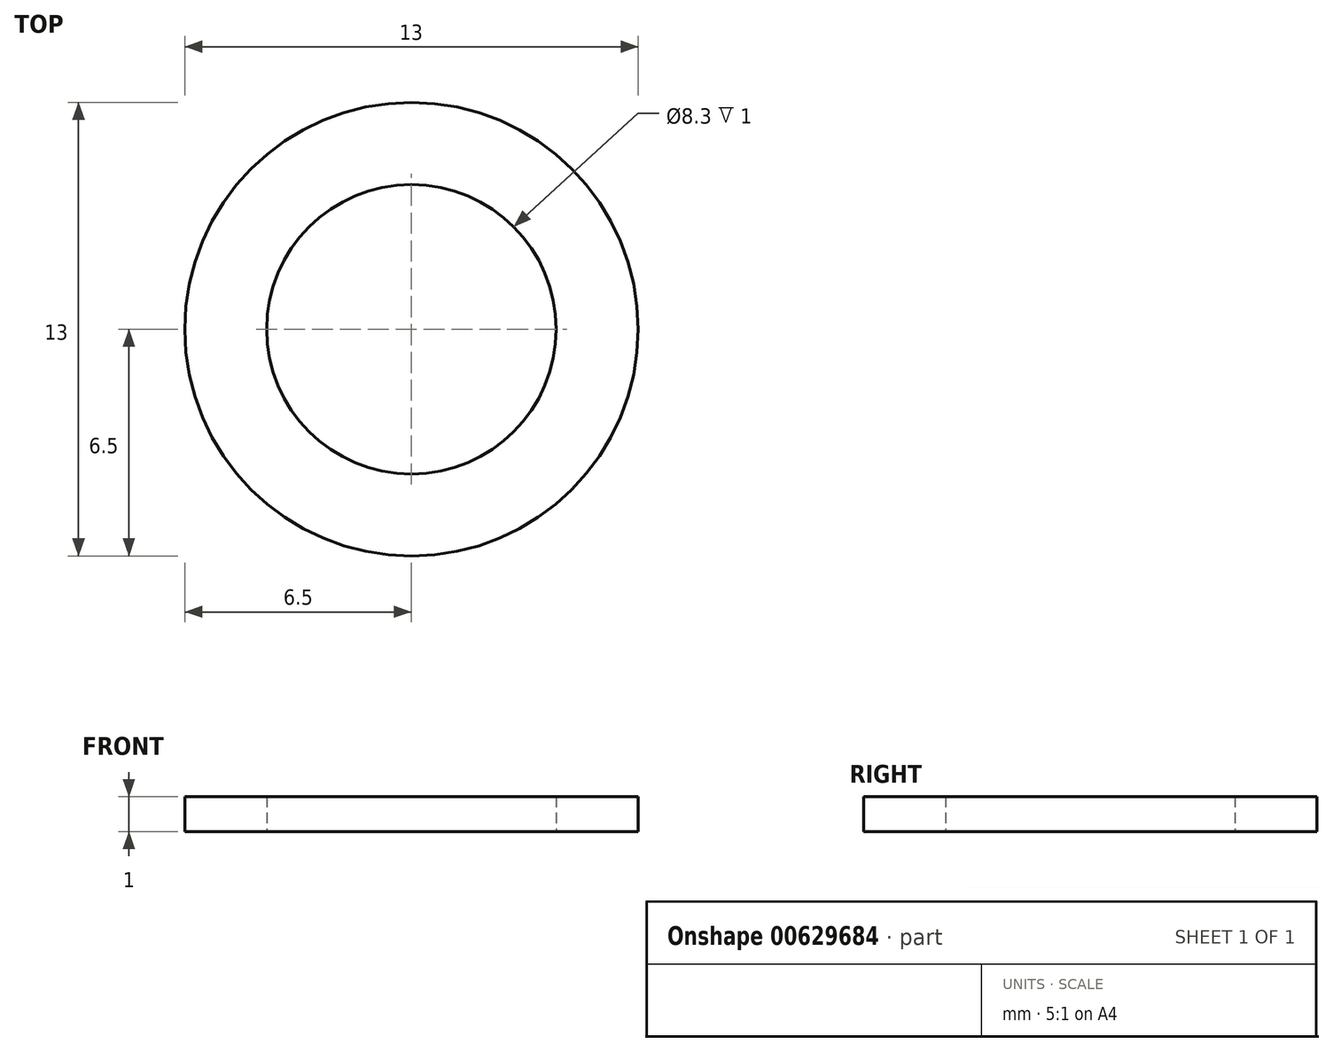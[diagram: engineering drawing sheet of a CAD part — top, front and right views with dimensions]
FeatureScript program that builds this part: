
annotation { "Feature Type Name" : "Feature", "Feature Type Description" : "" }
export const myFeature = defineFeature(function(context is Context, id is Id, definition is map)
    precondition{}
    {
        {
            var Q0;
            Q0=qCreatedBy(makeId("Top.planeOp"),FACE);
            var sketch = newSketch(context, id + "F0", { "sketchPlane" : qUnion([Q0])});
            skCircle(sketch, "E0", {"center": v(0, 0) * mm, "radius": 4.15 * mm});
            skCircle(sketch, "E1", {"center": v(0, 0) * mm, "radius": 6.5 * mm});
            skSolve(sketch);
        }
        {
            var Q0;
            Q0=makeQuery(id+"F0.imprint","IMPRINT",FACE,{"disambiguationData":[TD([[makeQuery(id+"F0.imprint","IMPRINT",EDGE,{"derivedFrom":sQuery(id+"F0.wireOp",EDGE,"E0")}),-1.0]])]});
            extrude(context, id + "F1", {"entities" : qUnion([Q0]), "depth" : 1 * mm, "offsetDistance" : 25.4 * mm});
        }
    });
